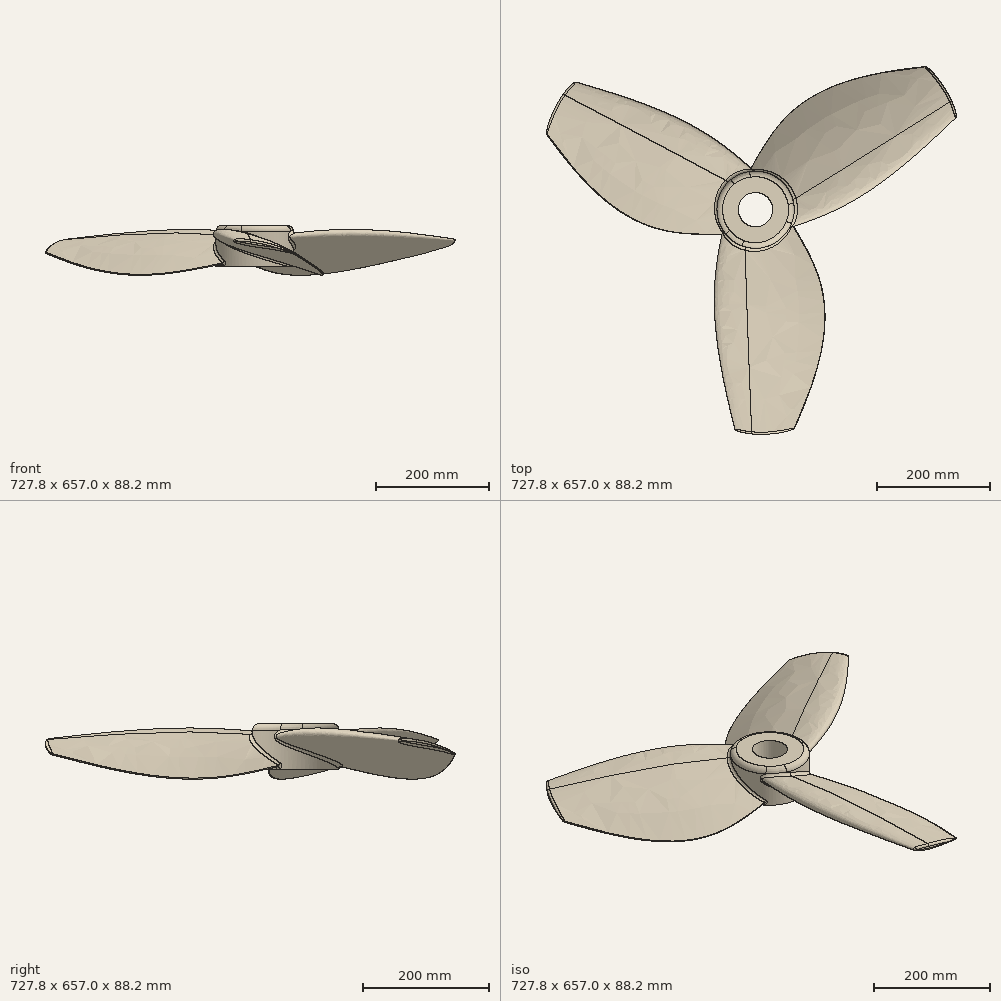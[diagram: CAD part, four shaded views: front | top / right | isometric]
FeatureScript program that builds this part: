
annotation { "Feature Type Name" : "Feature", "Feature Type Description" : "" }
export const myFeature = defineFeature(function(context is Context, id is Id, definition is map)
    precondition{}
    {
        {
            var Q0;
            Q0=qCreatedBy(makeId("Front.planeOp"),FACE);
            var sketch = newSketch(context, id + "F0", { "sketchPlane" : qUnion([Q0])});
            skLineSegment(sketch, "E0", {"start": v(-25.68, 10.16) * mm, "end": v(0, 0) * mm, "construction": true});
            skLineSegment(sketch, "E1", {"start": v(0, 0) * mm, "end": v(25.68, -10.16) * mm, "construction": true});
            skLineSegment(sketch, "E2", {"start": v(25.68, -10.16) * mm, "end": v(51.36, -20.31) * mm, "construction": true});
            skLineSegment(sketch, "E3", {"start": v(51.36, -20.31) * mm, "end": v(77.03, -30.47) * mm, "construction": true});
            skLineSegment(sketch, "E4", {"start": v(0, 0) * mm, "end": v(3.73, 9.44) * mm, "construction": true});
            skLineSegment(sketch, "E5", {"start": v(-25.68, 10.16) * mm, "end": v(-23.81, 14.88) * mm, "construction": true});
            skFitSpline(sketch, "E6", {"points": [v(-25.68, 10.16) * mm, v(3.73, 9.44) * mm, v(77.03, -30.47) * mm], "startDerivative": vector(15.03, 38) * mm, "endDerivative": vector(104.92, -93.69) * mm});
            skPoint(sketch, "E7", {"position": v(1.87, 4.72) * mm});
            skLineSegment(sketch, "E8", {"start": v(-23.81, 14.88) * mm, "end": v(1.87, 4.72) * mm, "construction": true});
            skLineSegment(sketch, "E9", {"start": v(0, 0) * mm, "end": v(-1.87, -4.72) * mm, "construction": true});
            skLineSegment(sketch, "E10", {"start": v(-25.68, 10.16) * mm, "end": v(-27.54, 5.44) * mm, "construction": true});
            skFitSpline(sketch, "E11", {"points": [v(-25.68, 10.16) * mm, v(-1.87, -4.72) * mm, v(77.03, -30.47) * mm], "startDerivative": vector(-15.23, -38.5) * mm, "endDerivative": vector(121.84, -48.19) * mm});
            skLineSegment(sketch, "E12", {"start": v(51.36, -20.31) * mm, "end": v(55.09, -10.87) * mm, "construction": true});
            skFitSpline(sketch, "E13", {"points": [v(9.98, -47.1) * mm, v(19.32, -41.32) * mm, v(25.33, -33.1) * mm, v(38.72, -38.94) * mm, v(51.52, -44.84) * mm], "startDerivative": vector(222.35, -194.18) * mm, "endDerivative": vector(45.97, -109.4) * mm});
            skSolve(sketch);
        }
        {
            var Q0;
            Q0=qCreatedBy(makeId("Front.planeOp"),FACE);
            cPlane(context, id + "F1", {"entities" : qUnion([Q0]), "cplaneType" : CPlaneType.OFFSET, "offset" : 125 * mm, "width" : 150 * mm, "height" : 150 * mm});
        }
        {
            var Q0;
            Q0=qCreatedBy(id+"F1.planeOp",FACE);
            var sketch = newSketch(context, id + "F2", { "sketchPlane" : qUnion([Q0])});
            skLineSegment(sketch, "E14", {"start": v(-47.25, 18.67) * mm, "end": v(0, 0) * mm, "construction": true});
            skLineSegment(sketch, "E15", {"start": v(0, 0) * mm, "end": v(47.25, -18.67) * mm, "construction": true});
            skLineSegment(sketch, "E16", {"start": v(47.25, -18.67) * mm, "end": v(94.5, -37.33) * mm, "construction": true});
            skLineSegment(sketch, "E17", {"start": v(94.5, -37.33) * mm, "end": v(141.75, -56) * mm, "construction": true});
            skLineSegment(sketch, "E18", {"start": v(0, 0) * mm, "end": v(7.35, 18.6) * mm, "construction": true});
            skLineSegment(sketch, "E19", {"start": v(-47.25, 18.67) * mm, "end": v(-43.58, 27.97) * mm, "construction": true});
            skFitSpline(sketch, "E20", {"points": [v(-47.25, 18.67) * mm, v(7.35, 18.6) * mm, v(141.75, -56) * mm], "startDerivative": vector(29.52, 74.71) * mm, "endDerivative": vector(191.05, -178.43) * mm});
            skPoint(sketch, "E21", {"position": v(3.67, 9.3) * mm});
            skLineSegment(sketch, "E22", {"start": v(-43.58, 27.97) * mm, "end": v(3.67, 9.3) * mm, "construction": true});
            skLineSegment(sketch, "E23", {"start": v(0, 0) * mm, "end": v(-3.67, -9.3) * mm, "construction": true});
            skLineSegment(sketch, "E24", {"start": v(-47.25, 18.67) * mm, "end": v(-50.92, 9.37) * mm, "construction": true});
            skFitSpline(sketch, "E25", {"points": [v(-47.25, 18.67) * mm, v(-3.67, -9.3) * mm, v(141.75, -56) * mm], "startDerivative": vector(-29.95, -75.82) * mm, "endDerivative": vector(224.28, -88.6) * mm});
            skLineSegment(sketch, "E26", {"start": v(94.5, -37.33) * mm, "end": v(101.85, -18.73) * mm, "construction": true});
            skSolve(sketch);
        }
        {
            var Q0;
            Q0=qCreatedBy(makeId("Front.planeOp"),FACE);
            cPlane(context, id + "F3", {"entities" : qUnion([Q0]), "cplaneType" : CPlaneType.OFFSET, "offset" : 400 * mm, "width" : 150 * mm, "height" : 150 * mm});
        }
        {
            var Q0;
            Q0=qCreatedBy(id+"F3.planeOp",FACE);
            var sketch = newSketch(context, id + "F4", { "sketchPlane" : qUnion([Q0])});
            skLineSegment(sketch, "E27", {"start": v(-10.03, 5.14) * mm, "end": v(16.27, 0) * mm, "construction": true});
            skLineSegment(sketch, "E28", {"start": v(16.27, 0) * mm, "end": v(42.56, -5.14) * mm, "construction": true});
            skLineSegment(sketch, "E29", {"start": v(42.56, -5.14) * mm, "end": v(68.86, -10.28) * mm, "construction": true});
            skLineSegment(sketch, "E30", {"start": v(68.86, -10.28) * mm, "end": v(95.16, -15.42) * mm, "construction": true});
            skLineSegment(sketch, "E31", {"start": v(16.27, 0) * mm, "end": v(17.61, 6.9) * mm, "construction": true});
            skLineSegment(sketch, "E32", {"start": v(-10.03, 5.14) * mm, "end": v(-9.36, 8.59) * mm, "construction": true});
            skFitSpline(sketch, "E33", {"points": [v(-10.03, 5.14) * mm, v(17.61, 6.9) * mm, v(95.16, -15.42) * mm], "startDerivative": vector(5.47, 28.01) * mm, "endDerivative": vector(118.7, -57.28) * mm});
            skPoint(sketch, "E34", {"position": v(16.94, 3.45) * mm});
            skLineSegment(sketch, "E35", {"start": v(-9.36, 8.59) * mm, "end": v(16.94, 3.45) * mm, "construction": true});
            skLineSegment(sketch, "E36", {"start": v(16.27, 0) * mm, "end": v(15.6, -3.45) * mm, "construction": true});
            skLineSegment(sketch, "E37", {"start": v(-10.03, 5.14) * mm, "end": v(-10.7, 1.7) * mm, "construction": true});
            skFitSpline(sketch, "E38", {"points": [v(-10.03, 5.14) * mm, v(15.6, -3.45) * mm, v(95.16, -15.42) * mm], "startDerivative": vector(-5.51, -28.2) * mm, "endDerivative": vector(124.61, -24.36) * mm});
            skLineSegment(sketch, "E39", {"start": v(68.86, -10.28) * mm, "end": v(70.2, -3.38) * mm, "construction": true});
            skSolve(sketch);
        }
        {
            var Q0;
            Q0=qSketchRegion(id+"F0",true);
            var Q1;
            Q1=qSketchRegion(id+"F2",true);
            var Q2;
            Q2=qSketchRegion(id+"F4",true);
            var Q3;
            Q3=sQuery(id+"F0.wireOp",VERTEX,"E6.1.internal");
            var Q4;
            Q4=sQuery(id+"F2.wireOp",VERTEX,"E20.1.internal");
            var Q5;
            Q5=sQuery(id+"F4.wireOp",VERTEX,"E31.end");
            loft(context, id + "F5", {"sheetProfilesArray" : [{ "sheetProfileEntities" : qUnion([Q0]) }, { "sheetProfileEntities" : qUnion([Q1]) }, { "sheetProfileEntities" : qUnion([Q2]) }], "matchConnections" : true, "connections" : [{ "connectionEntities" : qUnion([Q3, Q4, Q5]), "connectionEdgeQueries" : qUnion([]), "connectionEdgeParameters" : [] }]});
        }
        {
            var Q0;
            Q0=qCreatedBy(makeId("Top.planeOp"),FACE);
            var sketch = newSketch(context, id + "F6", { "sketchPlane" : qUnion([Q0])});
            skFitSpline(sketch, "E40", {"points": [v(-55.26, -360.76) * mm, v(38.24, -398.76) * mm, v(199.18, -336.71) * mm], "startDerivative": vector(111.22, -150.8) * mm, "endDerivative": vector(55.07, 148) * mm});
            skLineSegment(sketch, "E41", {"start": v(-55.26, -360.76) * mm, "end": v(-55.26, -458.75) * mm});
            skLineSegment(sketch, "E42", {"start": v(199.18, -336.71) * mm, "end": v(199.18, -458.75) * mm});
            skLineSegment(sketch, "E43", {"start": v(199.18, -458.75) * mm, "end": v(-55.26, -458.75) * mm});
            skSolve(sketch);
        }
        {
            var Q0;
            Q0=qSketchRegion(id+"F6",true);
            extrude(context, id + "F7", {"entities" : qUnion([Q0]), "operationType" : NewBodyOperationType.REMOVE, "endBound" : BoundingType.SYMMETRIC, "oppositeDirection" : true, "depth" : 40.17 * mm});
        }
        {
            var Q0;
            Q0=makeQuery(id+"F5.opLoft","SWEPT_EDGE",EDGE,{"disambiguationData":[OSD([sQuery(id+"F2.wireOp",EDGE,"E20"),sQuery(id+"F2.wireOp",EDGE,"E25"),sQuery(id+"F4.wireOp",EDGE,"E33"),sQuery(id+"F4.wireOp",EDGE,"E38")])]});
            fillet(context, id + "F8", {"entities" : qUnion([Q0]), "radius" : 1 * mm, "tangentPropagation" : true, "allowEdgeOverflow" : false});
        }
        {
            var Q0;
            Q0=makeQuery(id+"F7.boolean.opBoolean","COPY",FACE,{"derivedFrom":makeQuery(id+"F7.opExtrude","SWEPT_FACE",FACE,{"disambiguationData":[OSD([sQuery(id+"F6.wireOp",EDGE,"E40")])]})});
            fillet(context, id + "F9", {"entities" : qUnion([Q0]), "radius" : 4 * mm, "tangentPropagation" : true, "allowEdgeOverflow" : false});
        }
        {
            var Q0;
            Q0=qCreatedBy(makeId("Top.planeOp"),FACE);
            var sketch = newSketch(context, id + "F10", { "sketchPlane" : qUnion([Q0])});
            skCircle(sketch, "E44", {"center": v(24.35, 0) * mm, "radius": 68.6 * mm});
            skSolve(sketch);
        }
        {
            var Q0;
            Q0=qSketchRegion(id+"F10",true);
            extrude(context, id + "F11", {"entities" : qUnion([Q0]), "depth" : 32.31 * mm, "hasSecondDirection" : true, "secondDirectionOppositeDirection" : true, "secondDirectionDepth" : 40 * mm});
        }
        {
            var Q0;
            Q0=makeQuery(id+"F5.opLoft","SWEPT_BODY",BODY,{"disambiguationData":[OSD([makeQuery(id+"F0.imprint","IMPRINT",FACE,{"disambiguationData":[TD([[makeQuery(id+"F0.imprint","IMPRINT",EDGE,{"derivedFrom":sQuery(id+"F0.wireOp",EDGE,"E6")}),-1.0]])]}),sQuery(id+"F2.wireOp",EDGE,"E25"),makeQuery(id+"F4.imprint","IMPRINT",FACE,{"disambiguationData":[TD([[makeQuery(id+"F4.imprint","IMPRINT",EDGE,{"derivedFrom":sQuery(id+"F4.wireOp",EDGE,"E33")}),-1.0]])]})])]});
            var Q1;
            Q1=makeQuery(id+"F11.opExtrude","SWEPT_FACE",FACE,{"disambiguationData":[OSD([sQuery(id+"F10.wireOp",EDGE,"E44")])]});
            circularPattern(context, id + "F12", {"entities" : qUnion([Q0]), "axis" : qUnion([Q1]), "angle" : 360 * degree, "instanceCount" : 3, "equalSpace" : true});
        }
        {
            var Q0;
            Q0=makeQuery(id+"F12.opPattern","COPY",BODY,{"derivedFrom":makeQuery(id+"F5.opLoft","SWEPT_BODY",BODY,{"disambiguationData":[OSD([makeQuery(id+"F0.imprint","IMPRINT",FACE,{"disambiguationData":[TD([[makeQuery(id+"F0.imprint","IMPRINT",EDGE,{"derivedFrom":sQuery(id+"F0.wireOp",EDGE,"E6")}),-1.0]])]}),sQuery(id+"F2.wireOp",EDGE,"E25"),makeQuery(id+"F4.imprint","IMPRINT",FACE,{"disambiguationData":[TD([[makeQuery(id+"F4.imprint","IMPRINT",EDGE,{"derivedFrom":sQuery(id+"F4.wireOp",EDGE,"E33")}),-1.0]])]})])]}),"instanceName":"2"});
            var Q1;
            Q1=makeQuery(id+"F5.opLoft","SWEPT_BODY",BODY,{"disambiguationData":[OSD([makeQuery(id+"F0.imprint","IMPRINT",FACE,{"disambiguationData":[TD([[makeQuery(id+"F0.imprint","IMPRINT",EDGE,{"derivedFrom":sQuery(id+"F0.wireOp",EDGE,"E6")}),-1.0]])]}),sQuery(id+"F2.wireOp",EDGE,"E25"),makeQuery(id+"F4.imprint","IMPRINT",FACE,{"disambiguationData":[TD([[makeQuery(id+"F4.imprint","IMPRINT",EDGE,{"derivedFrom":sQuery(id+"F4.wireOp",EDGE,"E33")}),-1.0]])]})])]});
            var Q2;
            Q2=makeQuery(id+"F11.opExtrude","SWEPT_BODY",BODY,{"disambiguationData":[OSD([sQuery(id+"F10.wireOp",EDGE,"E44")])]});
            var Q3;
            Q3=makeQuery(id+"F12.opPattern","COPY",BODY,{"derivedFrom":makeQuery(id+"F5.opLoft","SWEPT_BODY",BODY,{"disambiguationData":[OSD([makeQuery(id+"F0.imprint","IMPRINT",FACE,{"disambiguationData":[TD([[makeQuery(id+"F0.imprint","IMPRINT",EDGE,{"derivedFrom":sQuery(id+"F0.wireOp",EDGE,"E6")}),-1.0]])]}),sQuery(id+"F2.wireOp",EDGE,"E25"),makeQuery(id+"F4.imprint","IMPRINT",FACE,{"disambiguationData":[TD([[makeQuery(id+"F4.imprint","IMPRINT",EDGE,{"derivedFrom":sQuery(id+"F4.wireOp",EDGE,"E33")}),-1.0]])]})])]}),"instanceName":"1"});
            var Q4;
            Q4=makeQuery(id+"F12.opPattern","COPY",BODY,{"derivedFrom":makeQuery(id+"F5.opLoft","SWEPT_BODY",BODY,{"disambiguationData":[OSD([makeQuery(id+"F0.imprint","IMPRINT",FACE,{"disambiguationData":[TD([[makeQuery(id+"F0.imprint","IMPRINT",EDGE,{"derivedFrom":sQuery(id+"F0.wireOp",EDGE,"E6")}),-1.0]])]}),sQuery(id+"F2.wireOp",EDGE,"E25"),makeQuery(id+"F4.imprint","IMPRINT",FACE,{"disambiguationData":[TD([[makeQuery(id+"F4.imprint","IMPRINT",EDGE,{"derivedFrom":sQuery(id+"F4.wireOp",EDGE,"E33")}),-1.0]])]})])]}),"instanceName":"4"});
            var Q5;
            Q5=makeQuery(id+"F12.opPattern","COPY",BODY,{"derivedFrom":makeQuery(id+"F5.opLoft","SWEPT_BODY",BODY,{"disambiguationData":[OSD([makeQuery(id+"F0.imprint","IMPRINT",FACE,{"disambiguationData":[TD([[makeQuery(id+"F0.imprint","IMPRINT",EDGE,{"derivedFrom":sQuery(id+"F0.wireOp",EDGE,"E6")}),-1.0]])]}),sQuery(id+"F2.wireOp",EDGE,"E25"),makeQuery(id+"F4.imprint","IMPRINT",FACE,{"disambiguationData":[TD([[makeQuery(id+"F4.imprint","IMPRINT",EDGE,{"derivedFrom":sQuery(id+"F4.wireOp",EDGE,"E33")}),-1.0]])]})])]}),"instanceName":"3"});
            booleanBodies(context, id + "F13", {"operationType" : BooleanOperationType.UNION, "tools" : qUnion([Q0, Q1, Q2, Q3, Q4, Q5])});
        }
        {
            var Q0;
            Q0=makeQuery(id+"F11.opExtrude","CAP_FACE",FACE,{"disambiguationData":[OSD([sQuery(id+"F10.wireOp",EDGE,"E44")])],"isStart":false});
            var sketch = newSketch(context, id + "F14", { "sketchPlane" : qUnion([Q0])});
            skCircle(sketch, "E45", {"center": v(24.35, 0) * mm, "radius": 30.45 * mm});
            skSolve(sketch);
        }
        {
            var Q0;
            Q0=qSketchRegion(id+"F14",true);
            extrude(context, id + "F15", {"entities" : qUnion([Q0]), "operationType" : NewBodyOperationType.REMOVE, "endBound" : BoundingType.THROUGH_ALL, "oppositeDirection" : true, "depth" : 25 * mm});
        }
        {
            var Q0;
            {var subQ0=sQuery(id+"F0.wireOp",VERTEX,"E6.1.internal");var subQ1=sQuery(id+"F0.wireOp",EDGE,"E6");var subQ2=sQuery(id+"F0.wireOp",EDGE,"E11");var subQ3=sQuery(id+"F2.wireOp",VERTEX,"E20.1.internal");var subQ4=sQuery(id+"F2.wireOp",EDGE,"E20");var subQ5=sQuery(id+"F2.wireOp",EDGE,"E25");Q0=makeQuery(id+"F13.opBoolean","INTERSECT",EDGE,{"derivedFrom":[makeQuery(id+"F11.opExtrude","SWEPT_FACE",FACE,{"disambiguationData":[OSD([sQuery(id+"F10.wireOp",EDGE,"E44")])]}),makeQuery(id+"F12.opPattern","COPY",FACE,{"derivedFrom":makeQuery(id+"F5.opLoft","SWEPT_FACE",FACE,{"disambiguationData":[OSD([subQ0,subQ1,subQ2,subQ3,subQ4,subQ5]),TDD([subQ0,makeQuery(id+"F0.imprint","INTERSECT",VERTEX,{"disambiguationData":[OD(0.0)],"derivedFrom":[subQ1,subQ2]}),makeQuery(id+"F0.imprint","IMPRINT",EDGE,{"derivedFrom":subQ1}),subQ3,makeQuery(id+"F2.imprint","INTERSECT",VERTEX,{"disambiguationData":[OD(0.0)],"derivedFrom":[subQ4,subQ5]}),makeQuery(id+"F2.imprint","IMPRINT",EDGE,{"derivedFrom":subQ4})])]}),"instanceName":"2"})]});}
            var Q1;
            {var subQ0=sQuery(id+"F0.wireOp",VERTEX,"E6.1.internal");var subQ1=sQuery(id+"F0.wireOp",EDGE,"E6");var subQ2=sQuery(id+"F0.wireOp",EDGE,"E11");var subQ3=sQuery(id+"F2.wireOp",VERTEX,"E20.1.internal");var subQ4=sQuery(id+"F2.wireOp",EDGE,"E20");var subQ5=sQuery(id+"F2.wireOp",EDGE,"E25");Q1=makeQuery(id+"F13.opBoolean","INTERSECT",EDGE,{"derivedFrom":[makeQuery(id+"F5.opLoft","SWEPT_FACE",FACE,{"disambiguationData":[OSD([subQ0,subQ1,subQ2,subQ3,subQ4,subQ5]),TDD([subQ0,makeQuery(id+"F0.imprint","INTERSECT",VERTEX,{"disambiguationData":[OD(1.0)],"derivedFrom":[subQ1,subQ2]}),makeQuery(id+"F0.imprint","IMPRINT",EDGE,{"derivedFrom":subQ1}),subQ3,makeQuery(id+"F2.imprint","INTERSECT",VERTEX,{"disambiguationData":[OD(1.0)],"derivedFrom":[subQ4,subQ5]}),makeQuery(id+"F2.imprint","IMPRINT",EDGE,{"derivedFrom":subQ4})])]}),makeQuery(id+"F11.opExtrude","SWEPT_FACE",FACE,{"disambiguationData":[OSD([sQuery(id+"F10.wireOp",EDGE,"E44")])]})]});}
            var Q2;
            {var subQ0=sQuery(id+"F0.wireOp",VERTEX,"E6.1.internal");var subQ1=sQuery(id+"F0.wireOp",EDGE,"E6");var subQ2=sQuery(id+"F0.wireOp",EDGE,"E11");var subQ3=sQuery(id+"F2.wireOp",VERTEX,"E20.1.internal");var subQ4=sQuery(id+"F2.wireOp",EDGE,"E20");var subQ5=sQuery(id+"F2.wireOp",EDGE,"E25");Q2=makeQuery(id+"F13.opBoolean","INTERSECT",EDGE,{"derivedFrom":[makeQuery(id+"F11.opExtrude","SWEPT_FACE",FACE,{"disambiguationData":[OSD([sQuery(id+"F10.wireOp",EDGE,"E44")])]}),makeQuery(id+"F12.opPattern","COPY",FACE,{"derivedFrom":makeQuery(id+"F5.opLoft","SWEPT_FACE",FACE,{"disambiguationData":[OSD([subQ0,subQ1,subQ2,subQ3,subQ4,subQ5]),TDD([subQ0,makeQuery(id+"F0.imprint","INTERSECT",VERTEX,{"disambiguationData":[OD(1.0)],"derivedFrom":[subQ1,subQ2]}),makeQuery(id+"F0.imprint","IMPRINT",EDGE,{"derivedFrom":subQ1}),subQ3,makeQuery(id+"F2.imprint","INTERSECT",VERTEX,{"disambiguationData":[OD(1.0)],"derivedFrom":[subQ4,subQ5]}),makeQuery(id+"F2.imprint","IMPRINT",EDGE,{"derivedFrom":subQ4})])]}),"instanceName":"1"})]});}
            var Q3;
            {var subQ0=sQuery(id+"F0.wireOp",VERTEX,"E6.1.internal");var subQ1=sQuery(id+"F0.wireOp",EDGE,"E6");var subQ2=sQuery(id+"F0.wireOp",EDGE,"E11");var subQ3=sQuery(id+"F2.wireOp",VERTEX,"E20.1.internal");var subQ4=sQuery(id+"F2.wireOp",EDGE,"E20");var subQ5=sQuery(id+"F2.wireOp",EDGE,"E25");Q3=makeQuery(id+"F13.opBoolean","INTERSECT",EDGE,{"derivedFrom":[makeQuery(id+"F11.opExtrude","SWEPT_FACE",FACE,{"disambiguationData":[OSD([sQuery(id+"F10.wireOp",EDGE,"E44")])]}),makeQuery(id+"F12.opPattern","COPY",FACE,{"derivedFrom":makeQuery(id+"F5.opLoft","SWEPT_FACE",FACE,{"disambiguationData":[OSD([subQ0,subQ1,subQ2,subQ3,subQ4,subQ5]),TDD([subQ0,makeQuery(id+"F0.imprint","INTERSECT",VERTEX,{"disambiguationData":[OD(1.0)],"derivedFrom":[subQ1,subQ2]}),makeQuery(id+"F0.imprint","IMPRINT",EDGE,{"derivedFrom":subQ1}),subQ3,makeQuery(id+"F2.imprint","INTERSECT",VERTEX,{"disambiguationData":[OD(1.0)],"derivedFrom":[subQ4,subQ5]}),makeQuery(id+"F2.imprint","IMPRINT",EDGE,{"derivedFrom":subQ4})])]}),"instanceName":"4"})]});}
            var Q4;
            {var subQ0=sQuery(id+"F0.wireOp",VERTEX,"E6.1.internal");var subQ1=sQuery(id+"F0.wireOp",EDGE,"E6");var subQ2=sQuery(id+"F0.wireOp",EDGE,"E11");var subQ3=sQuery(id+"F2.wireOp",VERTEX,"E20.1.internal");var subQ4=sQuery(id+"F2.wireOp",EDGE,"E20");var subQ5=sQuery(id+"F2.wireOp",EDGE,"E25");Q4=makeQuery(id+"F13.opBoolean","INTERSECT",EDGE,{"derivedFrom":[makeQuery(id+"F11.opExtrude","SWEPT_FACE",FACE,{"disambiguationData":[OSD([sQuery(id+"F10.wireOp",EDGE,"E44")])]}),makeQuery(id+"F12.opPattern","COPY",FACE,{"derivedFrom":makeQuery(id+"F5.opLoft","SWEPT_FACE",FACE,{"disambiguationData":[OSD([subQ0,subQ1,subQ2,subQ3,subQ4,subQ5]),TDD([subQ0,makeQuery(id+"F0.imprint","INTERSECT",VERTEX,{"disambiguationData":[OD(0.0)],"derivedFrom":[subQ1,subQ2]}),makeQuery(id+"F0.imprint","IMPRINT",EDGE,{"derivedFrom":subQ1}),subQ3,makeQuery(id+"F2.imprint","INTERSECT",VERTEX,{"disambiguationData":[OD(0.0)],"derivedFrom":[subQ4,subQ5]}),makeQuery(id+"F2.imprint","IMPRINT",EDGE,{"derivedFrom":subQ4})])]}),"instanceName":"3"})]});}
            fillet(context, id + "F16", {"entities" : qUnion([Q0, Q1, Q2, Q3, Q4]), "radius" : 5 * mm, "tangentPropagation" : true, "allowEdgeOverflow" : false});
        }
        {
            var Q0;
            Q0=makeQuery(id+"F11.opExtrude","CAP_EDGE",EDGE,{"disambiguationData":[OSD([sQuery(id+"F10.wireOp",EDGE,"E44")])],"isStart":false});
            fillet(context, id + "F17", {"entities" : qUnion([Q0]), "radius" : 10 * mm, "tangentPropagation" : true, "allowEdgeOverflow" : false});
        }
    });
